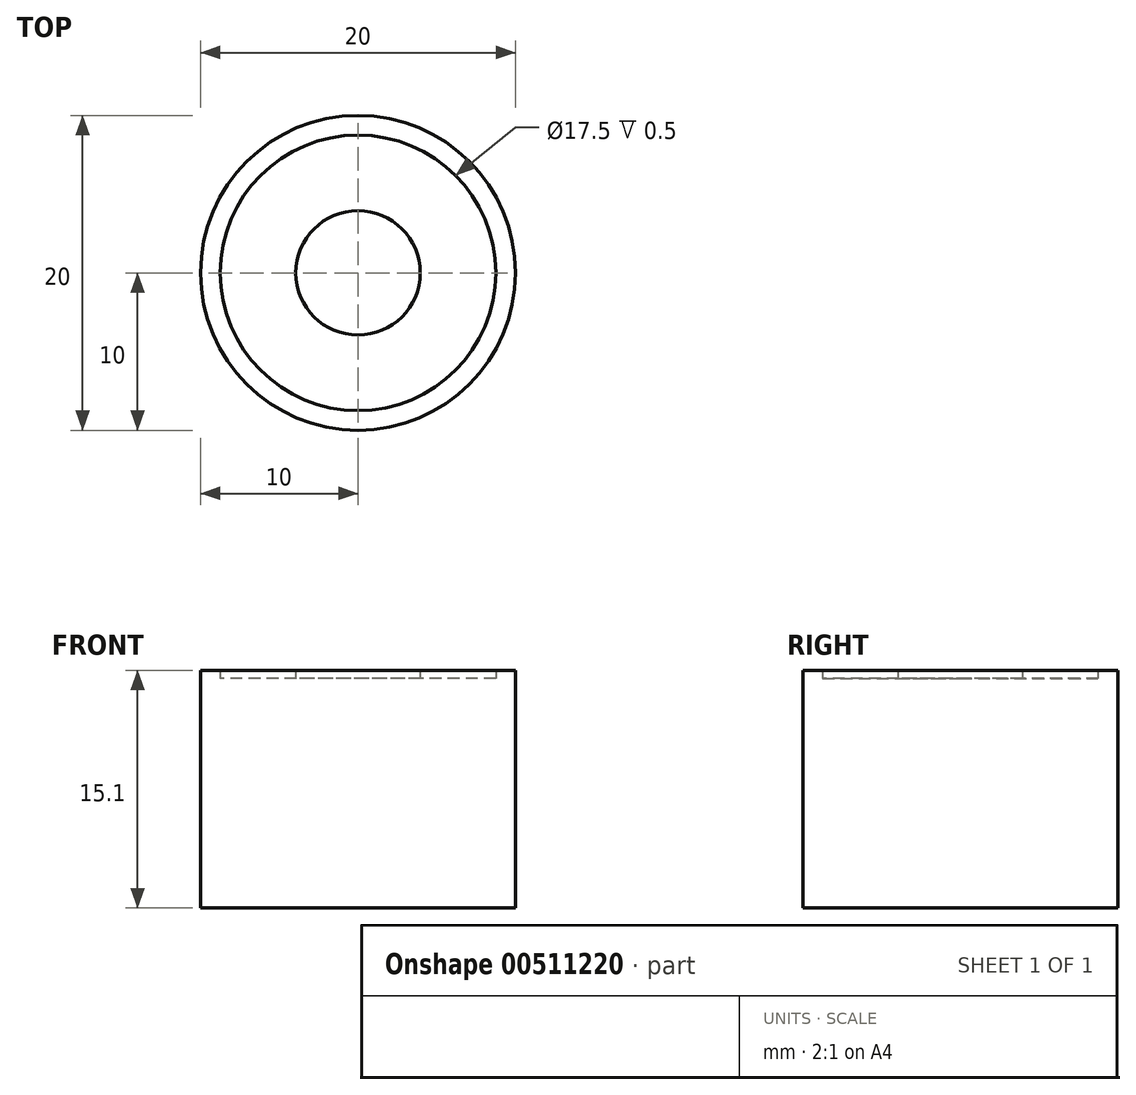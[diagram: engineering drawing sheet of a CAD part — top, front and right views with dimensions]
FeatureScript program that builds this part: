
annotation { "Feature Type Name" : "Feature", "Feature Type Description" : "" }
export const myFeature = defineFeature(function(context is Context, id is Id, definition is map)
    precondition{}
    {
        {
            var Q0;
            Q0=qCreatedBy(makeId("Top.planeOp"),FACE);
            var sketch = newSketch(context, id + "F0", { "sketchPlane" : qUnion([Q0])});
            skCircle(sketch, "E0", {"center": v(0, 0) * mm, "radius": 10 * mm});
            skCircle(sketch, "E1", {"center": v(0, 0) * mm, "radius": 3.95 * mm});
            skCircle(sketch, "E2", {"center": v(0, 0) * mm, "radius": 8.75 * mm});
            skSolve(sketch);
        }
        {
            var Q0;
            Q0 = qSketchRegion(id + "F0", true);
            var Q1;
            Q1=makeQuery(id+"F0.imprint","IMPRINT",FACE,{"disambiguationData":[TD([[makeQuery(id+"F0.imprint","IMPRINT",EDGE,{"derivedFrom":sQuery(id+"F0.wireOp",EDGE,"E1")}),1.0]])]});
            var Q2;
            Q2=makeQuery(id+"F0.imprint","IMPRINT",FACE,{"disambiguationData":[TD([[makeQuery(id+"F0.imprint","IMPRINT",EDGE,{"derivedFrom":sQuery(id+"F0.wireOp",EDGE,"E1")}),-1.0]])]});
            extrude(context, id + "F1", {"entities" : qUnion([Q0, Q1, Q2]), "oppositeDirection" : true, "depth" : 14.6 * mm});
        }
        {
            var Q0;
            Q0=makeQuery(id+"F0.imprint","IMPRINT",FACE,{"disambiguationData":[TD([[makeQuery(id+"F0.imprint","IMPRINT",EDGE,{"derivedFrom":sQuery(id+"F0.wireOp",EDGE,"E1")}),1.0]])]});
            var Q1;
            Q1=makeQuery(id+"F0.imprint","IMPRINT",FACE,{"disambiguationData":[TD([[makeQuery(id+"F0.imprint","IMPRINT",EDGE,{"derivedFrom":sQuery(id+"F0.wireOp",EDGE,"E0")}),1.0]])]});
            extrude(context, id + "F2", {"entities" : qUnion([Q0, Q1]), "operationType" : NewBodyOperationType.ADD, "depth" : 0.5 * mm});
        }
    });
